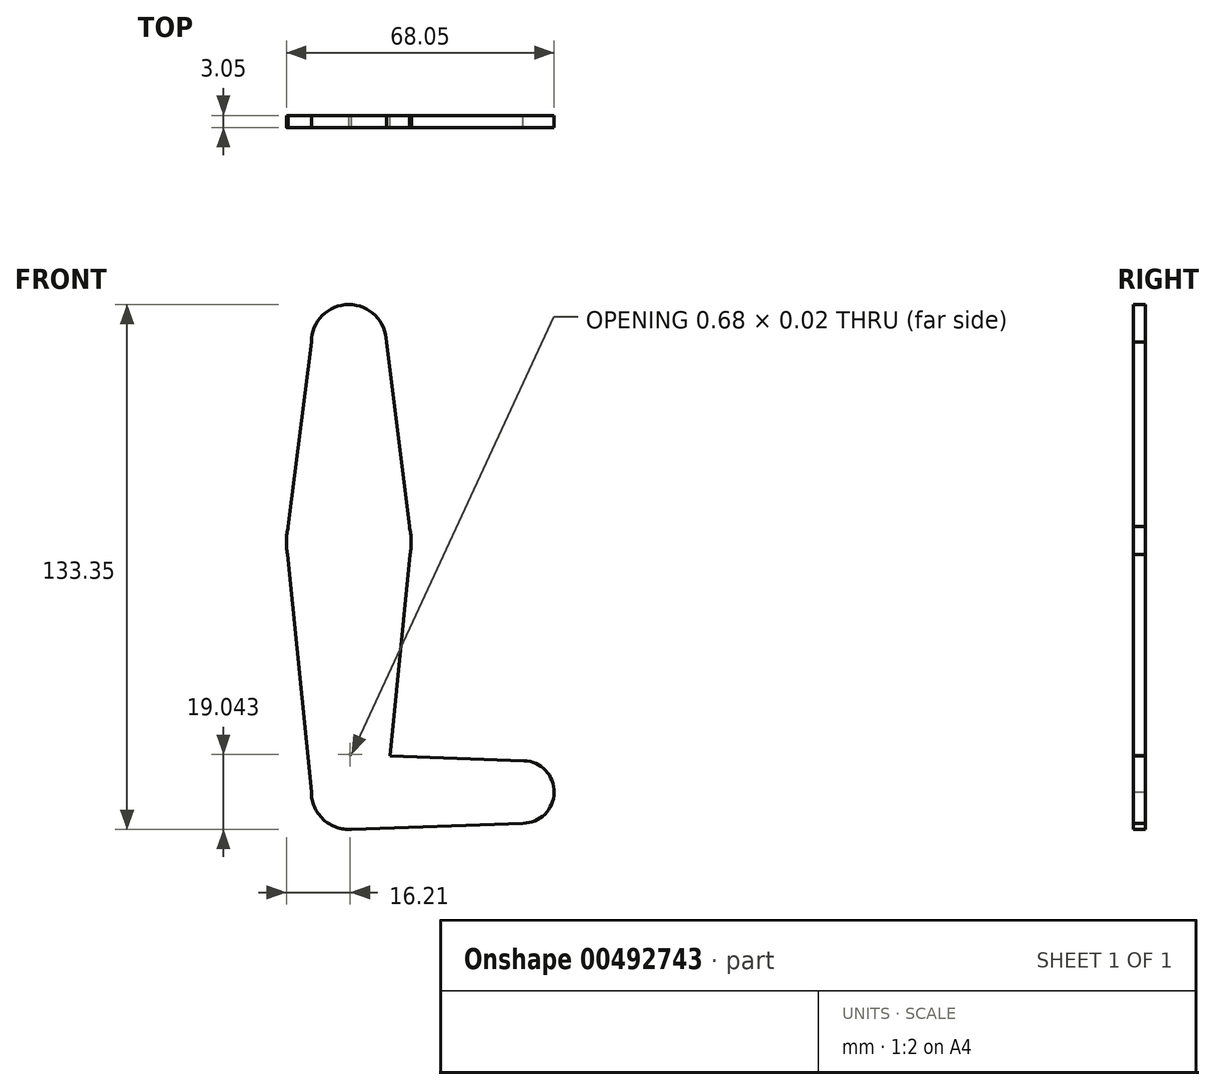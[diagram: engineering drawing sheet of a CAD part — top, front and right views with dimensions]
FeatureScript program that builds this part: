
annotation { "Feature Type Name" : "Feature", "Feature Type Description" : "" }
export const myFeature = defineFeature(function(context is Context, id is Id, definition is map)
    precondition{}
    {
        {
            var Q0;
            Q0=qCreatedBy(makeId("Front.planeOp"),FACE);
            var sketch = newSketch(context, id + "F0", { "sketchPlane" : qUnion([Q0])});
            skLineSegment(sketch, "E0", {"start": v(0, 0) * mm, "end": v(0, 114.3) * mm});
            skLineSegment(sketch, "E1", {"start": v(0, 0) * mm, "end": v(44.45, 0) * mm});
            skSolve(sketch);
        }
        {
            var Q0;
            Q0=qCreatedBy(makeId("Front.planeOp"),FACE);
            var sketch = newSketch(context, id + "F1", { "sketchPlane" : qUnion([Q0])});
            skCircle(sketch, "E2", {"center": v(0, 0) * mm, "radius": 9.53 * mm});
            skCircle(sketch, "E3", {"center": v(0, 114.3) * mm, "radius": 9.53 * mm});
            skLineSegment(sketch, "E4", {"start": v(0, 114.3) * mm, "end": v(0, 0) * mm, "construction": true});
            skLineSegment(sketch, "E5", {"start": v(0, 0) * mm, "end": v(44.24, 0) * mm, "construction": true});
            skCircle(sketch, "E6", {"center": v(44.24, 0) * mm, "radius": 7.94 * mm});
            skCircle(sketch, "E7", {"center": v(0, 63.5) * mm, "radius": 15.88 * mm});
            skLineSegment(sketch, "E8", {"start": v(0, 63.5) * mm, "end": v(0, 0) * mm, "construction": true});
            skLineSegment(sketch, "E9", {"start": v(0, 9.53) * mm, "end": v(44.53, 7.93) * mm});
            skLineSegment(sketch, "E10", {"start": v(0, -9.53) * mm, "end": v(44.24, -7.94) * mm});
            skLineSegment(sketch, "E11", {"start": v(-9.52, 114.3) * mm, "end": v(-15.87, 63.5) * mm});
            skLineSegment(sketch, "E12", {"start": v(9.52, 114.3) * mm, "end": v(15.88, 63.5) * mm});
            skLineSegment(sketch, "E13", {"start": v(-15.87, 63.5) * mm, "end": v(-9.53, 0) * mm});
            skLineSegment(sketch, "E14", {"start": v(15.88, 63.5) * mm, "end": v(9.53, 0) * mm});
            skSolve(sketch);
        }
        {
            var Q0;
            Q0=qCreatedBy(makeId("Front.planeOp"),FACE);
            var sketch = newSketch(context, id + "F2", { "sketchPlane" : qUnion([Q0])});
            skCircle(sketch, "E15", {"center": v(0, 114.29) * mm, "radius": 3.17 * mm});
            skCircle(sketch, "E16", {"center": v(0, 63.27) * mm, "radius": 3.18 * mm});
            skCircle(sketch, "E17", {"center": v(0, 0) * mm, "radius": 3.18 * mm});
            skCircle(sketch, "E18", {"center": v(44.3, 0.07) * mm, "radius": 3.18 * mm});
            skSolve(sketch);
        }
        {
            var Q0;
            Q0 = qSketchRegion(id + "F1", true);
            extrude(context, id + "F3", {"entities" : qUnion([Q0]), "depth" : 3.05 * mm});
        }
    });
